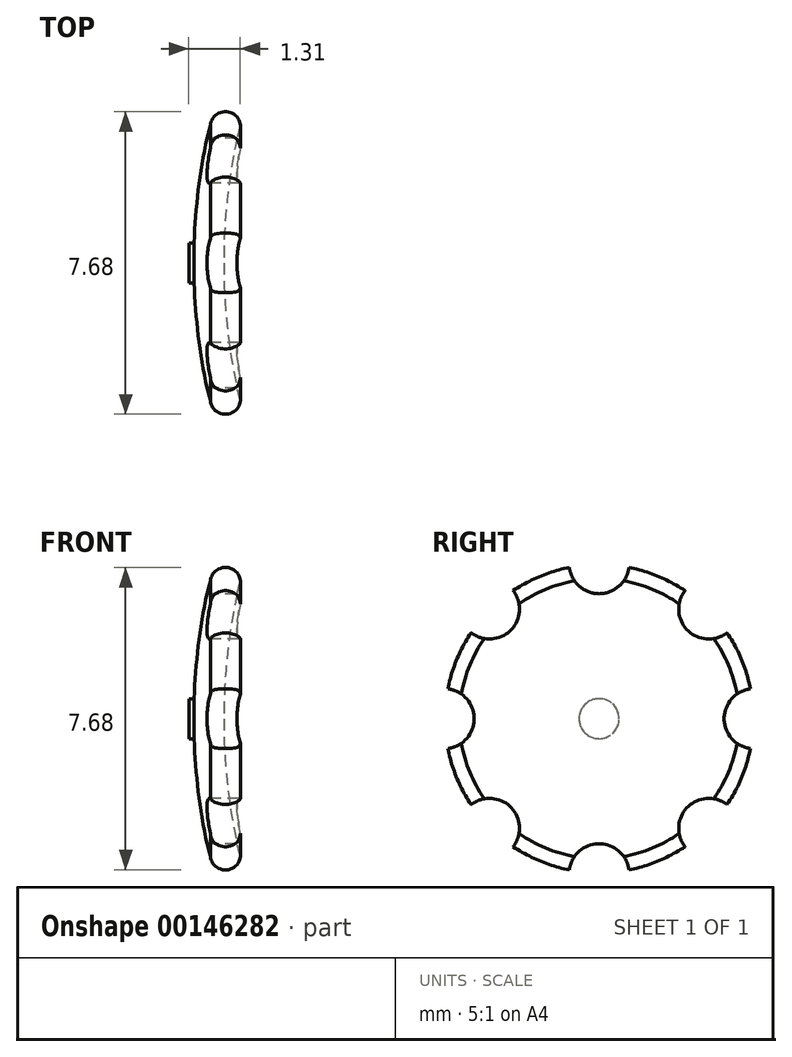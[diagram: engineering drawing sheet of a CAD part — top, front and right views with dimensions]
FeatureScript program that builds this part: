
annotation { "Feature Type Name" : "Feature", "Feature Type Description" : "" }
export const myFeature = defineFeature(function(context is Context, id is Id, definition is map)
    precondition{}
    {
        {
            var Q0;
            Q0=qCreatedBy(makeId("Front.planeOp"),FACE);
            var sketch = newSketch(context, id + "F0", { "sketchPlane" : qUnion([Q0])});
            skArc(sketch, "E0", {"start": v(0.42, 3.56) * mm, "mid": v(0.1, 1.8) * mm, "end": v(0, 0) * mm});
            skLineSegment(sketch, "E1", {"start": v(0, 0) * mm, "end": v(0.76, 0) * mm});
            skArc(sketch, "E2", {"start": v(1.18, 3.56) * mm, "mid": v(0.87, 1.8) * mm, "end": v(0.76, 0) * mm});
            skArc(sketch, "E3", {"start": v(1.18, 3.56) * mm, "mid": v(0.8, 3.92) * mm, "end": v(0.42, 3.56) * mm});
            skSolve(sketch);
        }
        {
            var Q0;
            Q0 = qSketchRegion(id + "F0", true);
            var Q1;
            Q1=sQuery(id+"F0.wireOp",EDGE,"E1");
            revolve(context, id + "F1", {"entities" : qUnion([Q0]), "axis" : qUnion([Q1]), "revolveType" : RevolveType.FULL});
        }
        {
            var Q0;
            Q0=qCreatedBy(makeId("Right.planeOp"),FACE);
            var sketch = newSketch(context, id + "F2", { "sketchPlane" : qUnion([Q0])});
            skLineSegment(sketch, "E4", {"start": v(0.76, 3.94) * mm, "end": v(-0.76, 3.94) * mm});
            skArc(sketch, "E5", {"start": v(-0.76, 3.94) * mm, "mid": v(0, 3.18) * mm, "end": v(0.76, 3.94) * mm});
            skArc(sketch, "E6.1.0", {"start": v(-3.32, 2.25) * mm, "mid": v(-2.25, 2.25) * mm, "end": v(-2.25, 3.32) * mm});
            skArc(sketch, "E6.2.0", {"start": v(-3.94, -0.76) * mm, "mid": v(-3.18, 0) * mm, "end": v(-3.94, 0.76) * mm});
            skArc(sketch, "E6.3.0", {"start": v(-2.25, -3.32) * mm, "mid": v(-2.25, -2.25) * mm, "end": v(-3.32, -2.25) * mm});
            skArc(sketch, "E6.4.0", {"start": v(0.76, -3.94) * mm, "mid": v(0, -3.18) * mm, "end": v(-0.76, -3.94) * mm});
            skArc(sketch, "E6.5.0", {"start": v(3.32, -2.25) * mm, "mid": v(2.25, -2.25) * mm, "end": v(2.25, -3.32) * mm});
            skArc(sketch, "E6.6.0", {"start": v(3.94, 0.76) * mm, "mid": v(3.18, 0) * mm, "end": v(3.94, -0.76) * mm});
            skArc(sketch, "E6.7.0", {"start": v(2.25, 3.32) * mm, "mid": v(2.25, 2.25) * mm, "end": v(3.32, 2.25) * mm});
            skPoint(sketch, "E6.center", {"position": v(0, 0) * mm});
            skLineSegment(sketch, "E7.1.0", {"start": v(-2.25, 3.32) * mm, "end": v(-3.32, 2.25) * mm});
            skLineSegment(sketch, "E7.2.0", {"start": v(-3.94, 0.76) * mm, "end": v(-3.94, -0.76) * mm});
            skLineSegment(sketch, "E7.3.0", {"start": v(-3.32, -2.25) * mm, "end": v(-2.25, -3.32) * mm});
            skLineSegment(sketch, "E7.4.0", {"start": v(-0.76, -3.94) * mm, "end": v(0.76, -3.94) * mm});
            skLineSegment(sketch, "E7.5.0", {"start": v(2.25, -3.32) * mm, "end": v(3.32, -2.25) * mm});
            skLineSegment(sketch, "E7.6.0", {"start": v(3.94, -0.76) * mm, "end": v(3.94, 0.76) * mm});
            skLineSegment(sketch, "E7.7.0", {"start": v(3.32, 2.25) * mm, "end": v(2.25, 3.32) * mm});
            skSolve(sketch);
        }
        {
            var Q0;
            Q0=makeQuery(id+"F2.imprint","IMPRINT",FACE,{"disambiguationData":[TD([[makeQuery(id+"F2.imprint","IMPRINT",EDGE,{"derivedFrom":sQuery(id+"F2.wireOp",EDGE,"E4")}),1.0]])]});
            var Q1;
            Q1=makeQuery(id+"F2.imprint","IMPRINT",FACE,{"disambiguationData":[TD([[makeQuery(id+"F2.imprint","IMPRINT",EDGE,{"derivedFrom":sQuery(id+"F2.wireOp",EDGE,"E6.9.0")}),1.0]])]});
            var Q2;
            Q2=makeQuery(id+"F2.imprint","IMPRINT",FACE,{"disambiguationData":[TD([[makeQuery(id+"F2.imprint","IMPRINT",EDGE,{"derivedFrom":sQuery(id+"F2.wireOp",EDGE,"E6.8.0")}),1.0]])]});
            var Q3;
            Q3=makeQuery(id+"F2.imprint","IMPRINT",FACE,{"disambiguationData":[TD([[makeQuery(id+"F2.imprint","IMPRINT",EDGE,{"derivedFrom":sQuery(id+"F2.wireOp",EDGE,"E6.7.0")}),1.0]])]});
            var Q4;
            Q4=makeQuery(id+"F2.imprint","IMPRINT",FACE,{"disambiguationData":[TD([[makeQuery(id+"F2.imprint","IMPRINT",EDGE,{"derivedFrom":sQuery(id+"F2.wireOp",EDGE,"E6.6.0")}),1.0]])]});
            var Q5;
            Q5=makeQuery(id+"F2.imprint","IMPRINT",FACE,{"disambiguationData":[TD([[makeQuery(id+"F2.imprint","IMPRINT",EDGE,{"derivedFrom":sQuery(id+"F2.wireOp",EDGE,"E6.5.0")}),1.0]])]});
            var Q6;
            Q6=makeQuery(id+"F2.imprint","IMPRINT",FACE,{"disambiguationData":[TD([[makeQuery(id+"F2.imprint","IMPRINT",EDGE,{"derivedFrom":sQuery(id+"F2.wireOp",EDGE,"E6.4.0")}),1.0]])]});
            var Q7;
            Q7=makeQuery(id+"F2.imprint","IMPRINT",FACE,{"disambiguationData":[TD([[makeQuery(id+"F2.imprint","IMPRINT",EDGE,{"derivedFrom":sQuery(id+"F2.wireOp",EDGE,"E6.3.0")}),1.0]])]});
            var Q8;
            Q8=makeQuery(id+"F2.imprint","IMPRINT",FACE,{"disambiguationData":[TD([[makeQuery(id+"F2.imprint","IMPRINT",EDGE,{"derivedFrom":sQuery(id+"F2.wireOp",EDGE,"E6.2.0")}),1.0]])]});
            var Q9;
            Q9=makeQuery(id+"F2.imprint","IMPRINT",FACE,{"disambiguationData":[TD([[makeQuery(id+"F2.imprint","IMPRINT",EDGE,{"derivedFrom":sQuery(id+"F2.wireOp",EDGE,"E6.1.0")}),1.0]])]});
            extrude(context, id + "F3", {"entities" : qUnion([Q0, Q1, Q2, Q3, Q4, Q5, Q6, Q7, Q8, Q9]), "operationType" : NewBodyOperationType.REMOVE, "depth" : 25.4 * mm});
        }
        {
            var Q0;
            Q0=qCreatedBy(makeId("Right.planeOp"),FACE);
            cPlane(context, id + "F4", {"entities" : qUnion([Q0]), "cplaneType" : CPlaneType.OFFSET, "offset" : 0.13 * mm, "width" : 152.4 * mm, "height" : 152.4 * mm});
        }
        {
            var Q0;
            Q0=qCreatedBy(id+"F4.planeOp",FACE);
            var sketch = newSketch(context, id + "F5", { "sketchPlane" : qUnion([Q0])});
            skCircle(sketch, "E8", {"center": v(0, 0) * mm, "radius": 0.5 * mm});
            skSolve(sketch);
        }
        {
            var Q0;
            Q0 = qSketchRegion(id + "F5", true);
            extrude(context, id + "F6", {"entities" : qUnion([Q0]), "operationType" : NewBodyOperationType.ADD, "oppositeDirection" : true, "depth" : 0.25 * mm});
        }
    });
